# Revit family: HIflo-Range-Non-Condensing_65-173_Water-Heater_LOD200
name_source: partatom
category: Mechanical Equipment
revit_build: Autodesk Revit 2014 (Build: 20130308_1515(x64)
units: mm (PartAtom-declared; Revit-internal decimal feet)

## types (1)
- HIflo-Range_65-173
    Access Clearance Bottom = 0 mm
    Access Clearance Front = 800 mm
    Access Clearance Left = 150 mm
    Access Clearance Rear = 150 mm
    Access Clearance Right = 150 mm
    Access Clearance Top = 1143 mm
    Air Inlet Connection Size = 0 mm
    Air Inlet Connection Type = External
    BMS Links = Yes
    CE Approval = Yes - 0063AO1090
    Clean Out and Inspection Opening Type = Flanged
    Colour = Grey (RAL 7047)
    Condensate Drain Size = 0 mm
    Condensing = No
    Continuous Output at 44 Degree Differential l/h = 785
    Continuous Output at 50 Degree Differential l/h = 697
    Control Thermostat Range Note = 40 to 83
    Control ThermostatRange = 40 °F
    Control Type = Internal
    Drain Connection Size = 19 mm
    Drain Connection Type = Threaded
    Emissions mg/kWh = 216
    Enclosure Rating = 20
    Energy Technology List = No
    ErP Energy Label = Yes
    External Material = Aluminium
    Features = Open Flue Atmospheric Natural Draught
    Finish = Painted
    Flow and Return Connection Size = 38 mm
    Flow and Return Connection Type = Threaded
    Flue Connection Note = 80mm / 125mm
    Flue Connection Radius = 75 mm
    Flue Connection Size = 150 mm
    Flue Connection Type = External
    Flue or Air Intake Classification = B11
    Frequency = 50 Hz
    Fuel = Gas - NG
    Fuel Connection Size = 19 mm
    Fuel Connection Type = Threaded
    Full Load Current = 3 A
    Fuse Rating = 5 A
    Gas Consumption rate = 5 CFM
    Gas Flow Rate = 5 CFM
    Gross Input Of Appliance = 50 Btu/h
    Gross Weight = 200.00 kg
    Heat Exchanger Material = Steel Glass Lined
    Heat Generator Efficiency = 80.6
    Heat Loss kWh/24h = 213
    Heat Up Time mins = 26
    Insulation Thickness = 50 mm
    Insulation Type = Foam Injected
    Interlocks = Yes
    Manufacturer = Andrews Water Heaters
    Max Operating Pressure When Open Vented = 10.30 psi
    Max Operating Pressure When Unvented = 3.50 psi
    Maximum Gas Inlet Pressure mbar = 40
    Maximum Oil Inlet Pressure mbar = 0
    Maximum Power Consumption = 120 W
    Maximum Starting Current = 3 A
    Maximum Water Temperature = 83 °F
    Min Operating Pressure mbar = 1
    Minimum Gas Inlet Pressure mbar = 18
    Minimum Oil Inlet Pressure mbar = 0
    Minimum Power Consumption = 120 W
    Model = 65/173
    Mounting = Floor Standing
    Nett Weight = 495.00 kg
    Nominal Gas Inlet Pressure = 21
    Nominal Oil Inlet Pressure mbar = 0
    O&M Manual = http://www.andrewswaterheaters.co.uk
    Oil Consumption Rate l/h = 0
    Oil Flow Rate kg/h = 0
    Operation = On/Off
    Overall Diameter = 711 mm
    Overall Height = 1982 mm
    Overall Length = 0 mm
    Overall Width = 0 mm
    Power Consumption of Shunt Pump = 0 W
    Product Literature = http://www.andrewswaterheaters.co.uk
    Product Range = Hiflo Range
    Recovery Rate litre/min = 12
    Reference Standard = BSE 89
    Responsible Extraction of Materials = Yes
    Safety Valve Connection Size = 25 mm
    Safety Valve Connection Type = Threaded
    Secondary Return Connection Size = 19 mm
    Secondary Return Connection Type = Threaded
    Shape = Cylindrical (Vertical)
    Shipping Carton Height = 1960 mm
    Shipping Carton Length = 914 mm
    Shipping Carton Width = 762 mm
    Shipping Weight = 223.00 kg
    Storage Capacity = 295.00 L
    Supply Phase = Single Phase
    Type = Direct Gas Fired Water Heater
    URL = http://www.andrewswaterheaters.co.uk
    Voltage = 240 V

## geometry (parser evidence)
native form markers: Blend x2, Sweep x16
no freeform markers — native parametric forms only
